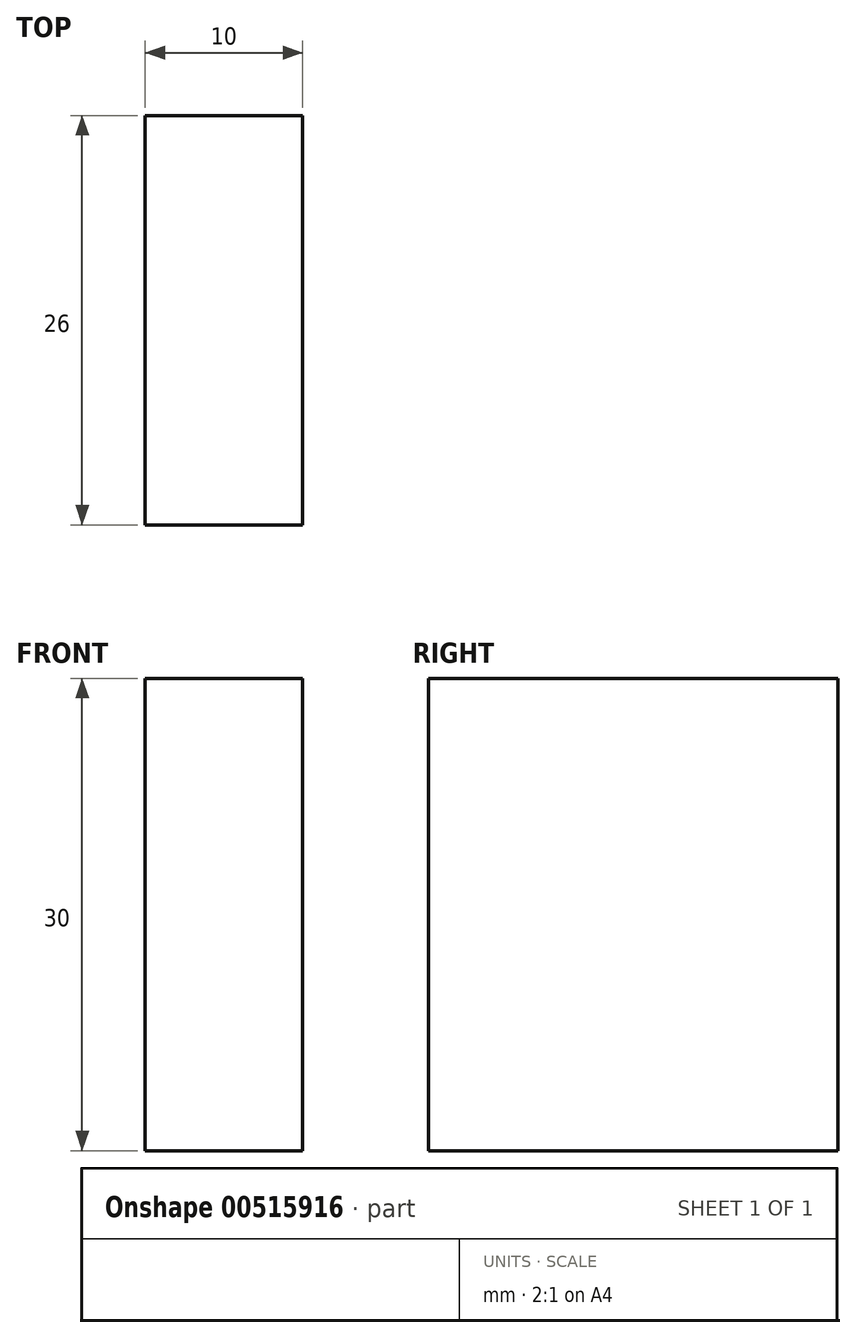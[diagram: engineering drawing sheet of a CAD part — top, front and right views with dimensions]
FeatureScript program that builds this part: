
annotation { "Feature Type Name" : "Feature", "Feature Type Description" : "" }
export const myFeature = defineFeature(function(context is Context, id is Id, definition is map)
    precondition{}
    {
        {
            var Q0;
            Q0=qCreatedBy(makeId("Top.planeOp"),FACE);
            var sketch = newSketch(context, id + "F0", { "sketchPlane" : qUnion([Q0])});
            skLineSegment(sketch, "E0", {"start": v(0, 0) * mm, "end": v(0, 26) * mm});
            skLineSegment(sketch, "E1", {"start": v(0, 26) * mm, "end": v(10, 26) * mm});
            skLineSegment(sketch, "E2", {"start": v(10, 26) * mm, "end": v(10, 0) * mm});
            skLineSegment(sketch, "E3", {"start": v(10, 0) * mm, "end": v(0, 0) * mm});
            skSolve(sketch);
        }
        {
            var Q0;
            Q0 = qSketchRegion(id + "F0", true);
            extrude(context, id + "F1", {"entities" : qUnion([Q0]), "depth" : 30 * mm, "offsetDistance" : 25 * mm});
        }
    });
